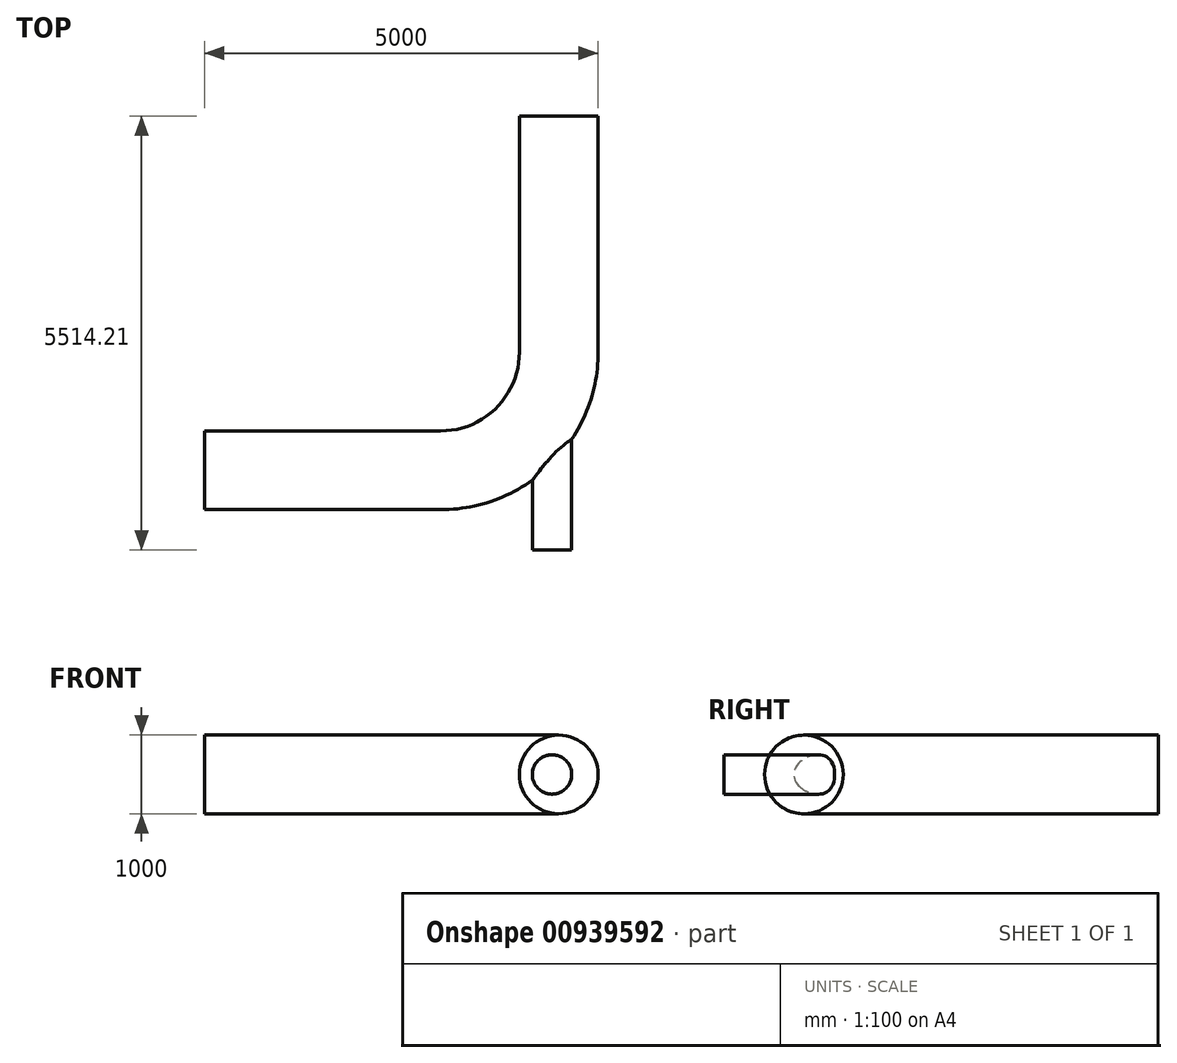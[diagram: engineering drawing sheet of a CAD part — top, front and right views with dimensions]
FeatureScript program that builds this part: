
annotation { "Feature Type Name" : "Feature", "Feature Type Description" : "" }
export const myFeature = defineFeature(function(context is Context, id is Id, definition is map)
    precondition{}
    {
        {
            var Q0;
            Q0=qCreatedBy(makeId("Top.planeOp"),FACE);
            var sketch = newSketch(context, id + "F0", { "sketchPlane" : qUnion([Q0])});
            skLineSegment(sketch, "E0", {"start": v(0, 0) * mm, "end": v(3000, 0) * mm});
            skArc(sketch, "E1", {"start": v(3000, 0) * mm, "mid": v(4060.66, 439.34) * mm, "end": v(4500, 1500) * mm});
            skLineSegment(sketch, "E2", {"start": v(4500, 1500) * mm, "end": v(4500, 4500) * mm});
            skArc(sketch, "E3.0", {"start": v(3000, -500) * mm, "mid": v(4414.21, 85.79) * mm, "end": v(5000, 1500) * mm, "construction": true});
            skLineSegment(sketch, "E4", {"start": v(3000, 1500) * mm, "end": v(4414.21, 85.79) * mm, "construction": true});
            skLineSegment(sketch, "E5", {"start": v(3000, 1500) * mm, "end": v(3000, -500) * mm, "construction": true});
            skLineSegment(sketch, "E6", {"start": v(4414.21, 85.79) * mm, "end": v(4414.21, -1014.21) * mm});
            skSolve(sketch);
        }
        {
            var Q0;
            Q0=qCreatedBy(makeId("Right.planeOp"),FACE);
            var sketch = newSketch(context, id + "F1", { "sketchPlane" : qUnion([Q0])});
            skCircle(sketch, "E7", {"center": v(0, 0) * mm, "radius": 500 * mm});
            skSolve(sketch);
        }
        {
            var Q0;
            Q0=makeQuery(id+"F1.imprint","IMPRINT",FACE,{"disambiguationData":[TD([[makeQuery(id+"F1.imprint","IMPRINT",EDGE,{"derivedFrom":sQuery(id+"F1.wireOp",EDGE,"E7")}),1.0]])]});
            var Q1;
            Q1=sQuery(id+"F0.wireOp",EDGE,"E0");
            var Q2;
            Q2=sQuery(id+"F0.wireOp",EDGE,"E1");
            var Q3;
            Q3=sQuery(id+"F0.wireOp",EDGE,"E2");
            sweep(context, id + "F2", {"profiles" : qUnion([Q0]), "path" : qUnion([Q1, Q2, Q3])});
        }
        {
            var Q0;
            Q0=sQuery(id+"F0.wireOp",EDGE,"E6");
            var Q1;
            Q1=sQuery(id+"F0.wireOp",VERTEX,"E6.end");
            cPlane(context, id + "F3", {"entities" : qUnion([Q0, Q1]), "cplaneType" : CPlaneType.LINE_POINT, "offset" : 25 * mm, "width" : 150 * mm, "height" : 150 * mm});
        }
        {
            var Q0;
            Q0=qCreatedBy(id+"F3.planeOp",FACE);
            var sketch = newSketch(context, id + "F4", { "sketchPlane" : qUnion([Q0])});
            skPoint(sketch, "E8.0", {"position": v(4414.21, 0) * mm});
            skCircle(sketch, "E9", {"center": v(4414.21, 0) * mm, "radius": 250 * mm});
            skSolve(sketch);
        }
        {
            var Q0;
            Q0=makeQuery(id+"F4.imprint","IMPRINT",FACE,{"disambiguationData":[TD([[makeQuery(id+"F4.imprint","IMPRINT",EDGE,{"derivedFrom":sQuery(id+"F4.wireOp",EDGE,"E9")}),1.0]])]});
            extrude(context, id + "F5", {"entities" : qUnion([Q0]), "operationType" : NewBodyOperationType.ADD, "oppositeDirection" : true, "depth" : 2620 * mm, "offsetDistance" : 25 * mm});
        }
    });
